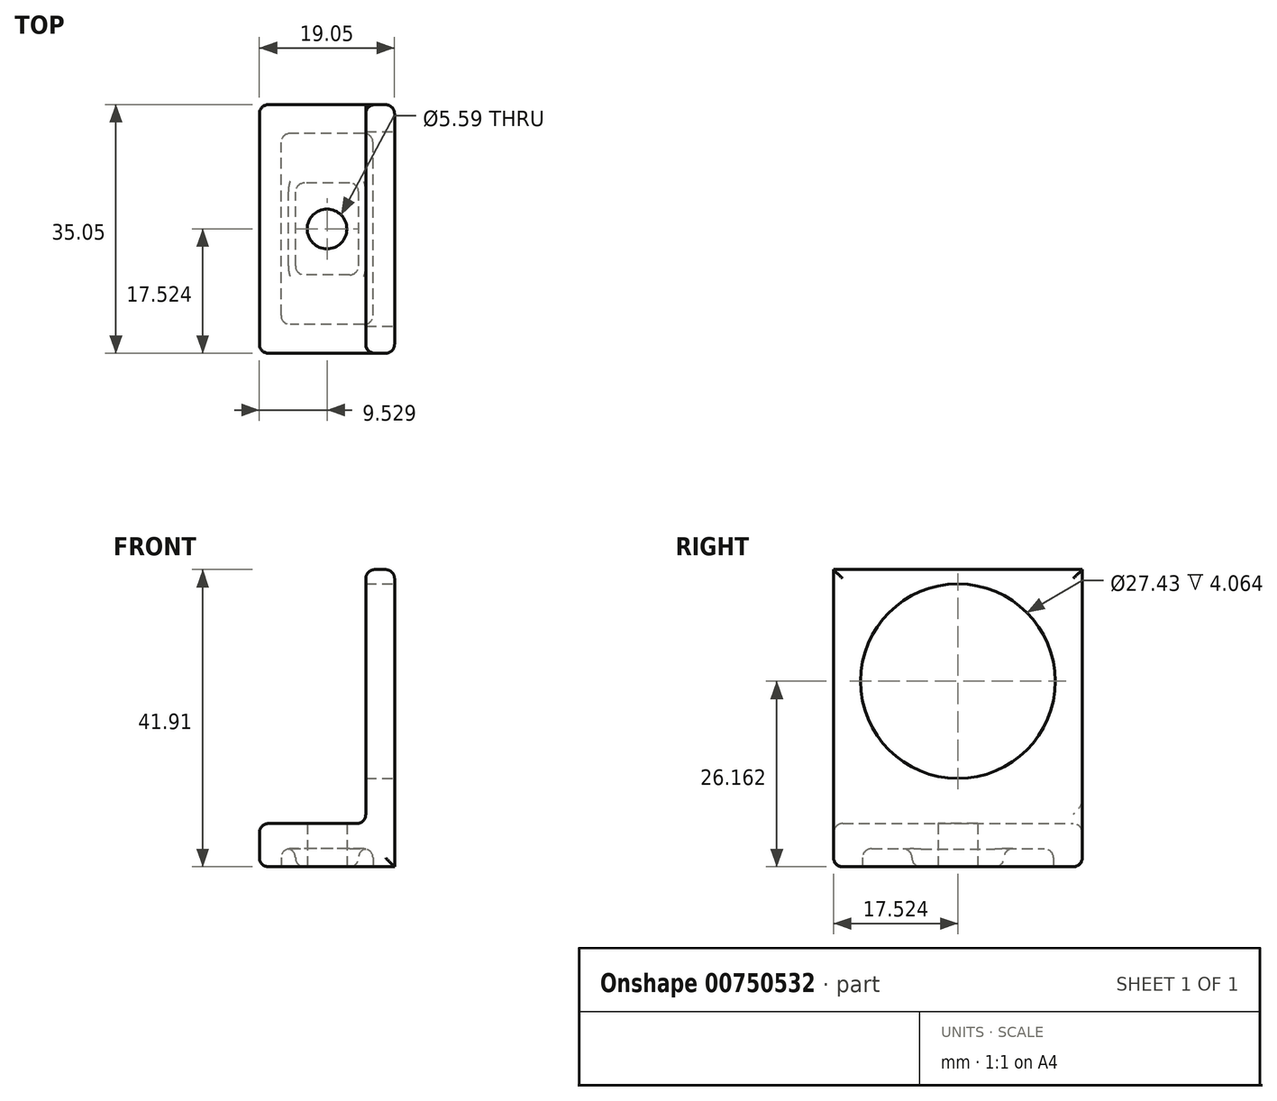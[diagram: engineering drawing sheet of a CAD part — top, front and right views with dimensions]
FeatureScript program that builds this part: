
annotation { "Feature Type Name" : "Feature", "Feature Type Description" : "" }
export const myFeature = defineFeature(function(context is Context, id is Id, definition is map)
    precondition{}
    {
        {
            var Q0;
            Q0=qCreatedBy(makeId("Front.planeOp"),FACE);
            var sketch = newSketch(context, id + "F0", { "sketchPlane" : qUnion([Q0])});
            skLineSegment(sketch, "E0.bottom", {"start": v(0, 0) * mm, "end": v(4.06, 0) * mm});
            skLineSegment(sketch, "E0.top", {"start": v(0, 41.91) * mm, "end": v(4.06, 41.91) * mm});
            skLineSegment(sketch, "E0.left", {"start": v(0, 0) * mm, "end": v(0, 41.91) * mm});
            skLineSegment(sketch, "E0.right", {"start": v(4.06, 0) * mm, "end": v(4.06, 41.91) * mm});
            skLineSegment(sketch, "E1.bottom", {"start": v(4.06, 0) * mm, "end": v(-14.99, 0) * mm});
            skLineSegment(sketch, "E1.top", {"start": v(4.06, 6.1) * mm, "end": v(-14.99, 6.1) * mm});
            skLineSegment(sketch, "E1.left", {"start": v(4.06, 0) * mm, "end": v(4.06, 6.1) * mm});
            skLineSegment(sketch, "E1.right", {"start": v(-14.99, 0) * mm, "end": v(-14.99, 6.1) * mm});
            skSolve(sketch);
        }
        {
            var Q0;
            Q0 = qSketchRegion(id + "F0", true);
            extrude(context, id + "F1", {"entities" : qUnion([Q0]), "depth" : 35.05 * mm, "offsetDistance" : 25.4 * mm});
        }
        {
            var Q0;
            Q0=makeQuery(id+"F1.opExtrude","SWEPT_FACE",FACE,{"disambiguationData":[OSD([sQuery(id+"F0.wireOp",EDGE,"E0.right"),sQuery(id+"F0.wireOp",EDGE,"E1.left")])]});
            var sketch = newSketch(context, id + "F2", { "sketchPlane" : qUnion([Q0])});
            skCircle(sketch, "E2", {"center": v(-17.53, 26.16) * mm, "radius": 13.72 * mm});
            skPoint(sketch, "E2.centerSnap0", {"position": v(-17.53, 41.91) * mm});
            skSolve(sketch);
        }
        {
            var Q0;
            Q0=makeQuery(id+"F2.imprint","IMPRINT",FACE,{"disambiguationData":[TD([[makeQuery(id+"F2.imprint","IMPRINT",EDGE,{"derivedFrom":sQuery(id+"F2.wireOp",EDGE,"E2")}),1.0]])]});
            extrude(context, id + "F3", {"entities" : qUnion([Q0]), "operationType" : NewBodyOperationType.REMOVE, "endBound" : BoundingType.THROUGH_ALL, "oppositeDirection" : true, "depth" : 25.4 * mm, "offsetDistance" : 25.4 * mm});
        }
        {
            var Q0;
            Q0=makeQuery(id+"F1.opExtrude","SWEPT_FACE",FACE,{"disambiguationData":[OSD([sQuery(id+"F0.wireOp",EDGE,"E1.bottom")])]});
            var sketch = newSketch(context, id + "F4", { "sketchPlane" : qUnion([Q0])});
            skCircle(sketch, "E3", {"center": v(-5.46, 17.53) * mm, "radius": 2.8 * mm});
            skPoint(sketch, "E3.centerSnap0", {"position": v(-5.46, 0) * mm});
            skPoint(sketch, "E3.centerSnap1", {"position": v(4.06, 17.53) * mm});
            skSolve(sketch);
        }
        {
            var Q0;
            Q0 = qSketchRegion(id + "F4", true);
            extrude(context, id + "F5", {"entities" : qUnion([Q0]), "operationType" : NewBodyOperationType.REMOVE, "endBound" : BoundingType.THROUGH_ALL, "oppositeDirection" : true, "depth" : 25.4 * mm, "offsetDistance" : 25.4 * mm});
        }
        {
            var Q0;
            Q0=makeQuery(id+"F1.opExtrude","SWEPT_FACE",FACE,{"disambiguationData":[OSD([sQuery(id+"F0.wireOp",EDGE,"E1.bottom")])]});
            var sketch = newSketch(context, id + "F6", { "sketchPlane" : qUnion([Q0])});
            skLineSegment(sketch, "E4.bottom", {"start": v(-2.29, 24) * mm, "end": v(-8.64, 24) * mm});
            skLineSegment(sketch, "E4.top", {"start": v(-2.29, 11.05) * mm, "end": v(-8.64, 11.05) * mm});
            skLineSegment(sketch, "E4.left", {"start": v(-1.02, 22.73) * mm, "end": v(-1.02, 12.32) * mm});
            skLineSegment(sketch, "E4.right", {"start": v(-9.9, 22.73) * mm, "end": v(-9.9, 12.32) * mm});
            skLineSegment(sketch, "E5.bottom", {"start": v(-0.25, 30.99) * mm, "end": v(-10.67, 30.99) * mm});
            skLineSegment(sketch, "E5.top", {"start": v(-0.25, 4.06) * mm, "end": v(-10.67, 4.06) * mm});
            skLineSegment(sketch, "E5.left", {"start": v(1.02, 29.72) * mm, "end": v(1.02, 5.33) * mm});
            skLineSegment(sketch, "E5.right", {"start": v(-11.94, 29.72) * mm, "end": v(-11.94, 5.33) * mm});
            skPoint(sketch, "E6.visualSharp", {"position": v(1.02, 30.99) * mm});
            skArc(sketch, "E6.filletArc", {"start": v(1.02, 29.72) * mm, "mid": v(0.64, 30.62) * mm, "end": v(-0.25, 30.99) * mm});
            skPoint(sketch, "E7.visualSharp", {"position": v(1.02, 4.06) * mm});
            skArc(sketch, "E7.filletArc", {"start": v(-0.25, 4.06) * mm, "mid": v(0.64, 4.44) * mm, "end": v(1.02, 5.33) * mm});
            skPoint(sketch, "E8.visualSharp", {"position": v(-11.94, 4.06) * mm});
            skArc(sketch, "E8.filletArc", {"start": v(-11.94, 5.33) * mm, "mid": v(-11.57, 4.44) * mm, "end": v(-10.67, 4.06) * mm});
            skPoint(sketch, "E9.visualSharp", {"position": v(-11.94, 30.99) * mm});
            skArc(sketch, "E9.filletArc", {"start": v(-10.67, 30.99) * mm, "mid": v(-11.57, 30.62) * mm, "end": v(-11.94, 29.72) * mm});
            skPoint(sketch, "E10.visualSharp", {"position": v(-9.9, 24) * mm});
            skArc(sketch, "E10.filletArc", {"start": v(-8.64, 24) * mm, "mid": v(-9.53, 23.63) * mm, "end": v(-9.9, 22.73) * mm});
            skPoint(sketch, "E11.visualSharp", {"position": v(-1.02, 24) * mm});
            skArc(sketch, "E11.filletArc", {"start": v(-1.02, 22.73) * mm, "mid": v(-1.39, 23.63) * mm, "end": v(-2.29, 24) * mm});
            skPoint(sketch, "E12.visualSharp", {"position": v(-1.02, 11.05) * mm});
            skArc(sketch, "E12.filletArc", {"start": v(-2.29, 11.05) * mm, "mid": v(-1.39, 11.42) * mm, "end": v(-1.02, 12.32) * mm});
            skPoint(sketch, "E13.visualSharp", {"position": v(-9.9, 11.05) * mm});
            skArc(sketch, "E13.filletArc", {"start": v(-9.9, 12.32) * mm, "mid": v(-9.53, 11.42) * mm, "end": v(-8.64, 11.05) * mm});
            skSolve(sketch);
        }
        {
            var Q0;
            Q0=makeQuery(id+"F6.imprint","IMPRINT",FACE,{"disambiguationData":[TD([[makeQuery(id+"F6.imprint","IMPRINT",EDGE,{"derivedFrom":sQuery(id+"F6.wireOp",EDGE,"E4.bottom")}),-1.0]])]});
            extrude(context, id + "F7", {"entities" : qUnion([Q0]), "operationType" : NewBodyOperationType.REMOVE, "oppositeDirection" : true, "depth" : 2.54 * mm, "offsetDistance" : 25.4 * mm});
        }
        {
            var Q0;
            Q0=makeQuery(id+"F7.boolean.opBoolean","COPY",EDGE,{"derivedFrom":makeQuery(id+"F7.opExtrude","CAP_EDGE",EDGE,{"disambiguationData":[OSD([sQuery(id+"F6.wireOp",EDGE,"E5.left")])],"isStart":true})});
            var Q1;
            Q1=makeQuery(id+"F7.boolean.opBoolean","COPY",EDGE,{"derivedFrom":makeQuery(id+"F7.opExtrude","CAP_EDGE",EDGE,{"disambiguationData":[OSD([sQuery(id+"F6.wireOp",EDGE,"E4.left")])],"isStart":true})});
            var Q2;
            Q2=makeQuery(id+"F7.boolean.opBoolean","COPY",EDGE,{"derivedFrom":makeQuery(id+"F7.opExtrude","CAP_EDGE",EDGE,{"disambiguationData":[OSD([sQuery(id+"F6.wireOp",EDGE,"E5.left")])],"isStart":false})});
            var Q3;
            Q3=makeQuery(id+"F7.boolean.opBoolean","COPY",EDGE,{"derivedFrom":makeQuery(id+"F7.opExtrude","CAP_EDGE",EDGE,{"disambiguationData":[OSD([sQuery(id+"F6.wireOp",EDGE,"E4.top")])],"isStart":false})});
            var Q4;
            Q4=makeQuery(id+"F1.opExtrude","CAP_EDGE",EDGE,{"disambiguationData":[OSD([sQuery(id+"F0.wireOp",EDGE,"E1.bottom")])],"isStart":true});
            var Q5;
            Q5=makeQuery(id+"F1.opExtrude","SWEPT_EDGE",EDGE,{"disambiguationData":[OSD([sQuery(id+"F0.wireOp",EDGE,"E1.bottom"),sQuery(id+"F0.wireOp",EDGE,"E1.right")])]});
            var Q6;
            Q6=makeQuery(id+"F1.opExtrude","CAP_EDGE",EDGE,{"disambiguationData":[OSD([sQuery(id+"F0.wireOp",EDGE,"E1.bottom")])],"isStart":false});
            var Q7;
            Q7=makeQuery(id+"F1.opExtrude","SWEPT_EDGE",EDGE,{"disambiguationData":[OSD([sQuery(id+"F0.wireOp",EDGE,"E1.bottom"),sQuery(id+"F0.wireOp",EDGE,"E1.left")])]});
            var Q8;
            Q8=makeQuery(id+"F1.opExtrude","SWEPT_EDGE",EDGE,{"disambiguationData":[OSD([sQuery(id+"F0.wireOp",EDGE,"E0.top"),sQuery(id+"F0.wireOp",EDGE,"E0.left")])]});
            var Q9;
            Q9=makeQuery(id+"F1.opExtrude","CAP_EDGE",EDGE,{"disambiguationData":[OSD([sQuery(id+"F0.wireOp",EDGE,"E1.right")])],"isStart":true});
            var Q10;
            Q10=makeQuery(id+"F1.opExtrude","CAP_EDGE",EDGE,{"disambiguationData":[OSD([sQuery(id+"F0.wireOp",EDGE,"E1.right")])],"isStart":false});
            var Q11;
            Q11=makeQuery(id+"F1.opExtrude","CAP_EDGE",EDGE,{"disambiguationData":[OSD([sQuery(id+"F0.wireOp",EDGE,"E1.top")])],"isStart":false});
            var Q12;
            Q12=makeQuery(id+"F1.opExtrude","SWEPT_EDGE",EDGE,{"disambiguationData":[OSD([sQuery(id+"F0.wireOp",EDGE,"E1.top"),sQuery(id+"F0.wireOp",EDGE,"E1.right")])]});
            var Q13;
            Q13=makeQuery(id+"F1.opExtrude","CAP_EDGE",EDGE,{"disambiguationData":[OSD([sQuery(id+"F0.wireOp",EDGE,"E1.top")])],"isStart":true});
            var Q14;
            Q14=makeQuery(id+"F1.opExtrude","SWEPT_EDGE",EDGE,{"disambiguationData":[OSD([sQuery(id+"F0.wireOp",EDGE,"E0.left"),sQuery(id+"F0.wireOp",EDGE,"E1.top")])]});
            var Q15;
            Q15=makeQuery(id+"F1.opExtrude","CAP_EDGE",EDGE,{"disambiguationData":[OSD([sQuery(id+"F0.wireOp",EDGE,"E0.left")])],"isStart":false});
            var Q16;
            Q16=makeQuery(id+"F1.opExtrude","SWEPT_EDGE",EDGE,{"disambiguationData":[OSD([sQuery(id+"F0.wireOp",EDGE,"E0.top"),sQuery(id+"F0.wireOp",EDGE,"E0.right")])]});
            var Q17;
            Q17=makeQuery(id+"F1.opExtrude","CAP_EDGE",EDGE,{"disambiguationData":[OSD([sQuery(id+"F0.wireOp",EDGE,"E0.right"),sQuery(id+"F0.wireOp",EDGE,"E1.left")])],"isStart":true});
            var Q18;
            Q18=makeQuery(id+"F1.opExtrude","CAP_EDGE",EDGE,{"disambiguationData":[OSD([sQuery(id+"F0.wireOp",EDGE,"E0.right"),sQuery(id+"F0.wireOp",EDGE,"E1.left")])],"isStart":false});
            fillet(context, id + "F8", {"entities" : qUnion([Q0, Q1, Q2, Q3, Q4, Q5, Q6, Q7, Q8, Q9, Q10, Q11, Q12, Q13, Q14, Q15, Q16, Q17, Q18]), "radius" : 1.27 * mm, "tangentPropagation" : true, "allowEdgeOverflow" : false});
        }
    });
